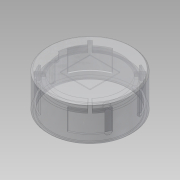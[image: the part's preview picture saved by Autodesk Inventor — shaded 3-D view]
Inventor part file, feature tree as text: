
AUTODESK INVENTOR PART (.ipt)
format: ipt  version: 2015 SP2 (Build 190223200, 223)  size: 409,600 bytes
history: native  units: mm
features: other x6, sketch x6, extrude x5, chamfer x4, projected_geometry x3, revolve x2, plane x2, pattern_circular x2
ambient origin geometry x8: Origin, YZ Plane, XZ Plane, XY Plane, X Axis, Y Axis, Z Axis, Center Point
bodies: Solid1 (feature_tree)
feature tree (30):
  other  "CrossSection1"
  other  "CrossSection2"
  other  "CrossSection3"
  other  "CrossSection4"
  other  "CrossSection5"
  revolve  "Revolution1"  Angle=90.0deg
  plane  "Work Plane3"
  chamfer  "Chamfer1"  Distance=7.75mm
  extrude  "Extrusion3"  Depth=4.363323mm
  extrude  "Extrusion1"  Depth=1.8mm
  extrude  "Extrusion6"  Depth=10.0mm
  plane  "Work Plane1"
  other  "Work Axis1"
  revolve  "Revolution2"  [1 undecoded]
  pattern_circular  "Circular Pattern1"  [2 undecoded]
  extrude  "Extrusion7"  Depth=10.0mm
  pattern_circular  "Circular Pattern3"  Count=4 Angle=360.0deg
  chamfer  "Chamfer2"  Distance=1.0mm
  extrude  "Extrusion10"  Depth=10.0mm
  chamfer  "Chamfer3"  Distance=1.5mm
  chamfer  "Chamfer4"  Distance=1.25mm
  sketch  "Sketch2"  dims[d3=12.0mm d4=90.0deg]
  sketch  "Sketch3"  dims[d5=28.0mm d15=7.75mm d16=0.0mm]
  sketch  "Sketch7"  dims[d17=4.363323mm d18=4.363323mm]
  sketch  "Sketch9"  dims[d21=0.5mm d22=2.0mm d23=45.0deg d33=1.8mm]
  sketch  "Sketch16"  dims[d35=10.0mm d36=10.0mm]
  projected_geometry  "Projected Loop2"
  projected_geometry  "Projected Loop4"
  sketch  "Sketch19"  dims[d37=0.25mm d38=0.0mm d48=0.5mm d49=2.0mm d50=7.0mm d51=20.0mm d52=0.5mm d53=2.0mm d54=0.0mm d55=20.0mm d59=0.5mm d60=7.0mm d63=8.37758mm d65=40.0mm d66=360.0deg d81=0.5mm d82=2.0mm d83=0.0mm d84=20.0mm d85=0.5mm d86=2.0mm d87=2.5mm d88=20.0mm d89=0.5mm d90=2.0mm d91=2.5mm d92=20.0mm d100=1.0mm d113=1.0mm d119=1.5mm d120=1.25mm d121=4.363323mm d122=4.363323mm d123=6.75mm d124=0.0mm d127=0.872665mm d128=0.436332mm d129=0.872665mm d130=6.75mm d131=0.0mm d132=40.0mm d133=360.0deg d135=0.125mm d136=0.25mm d137=45.0deg d140=21.0mm d141=23.0mm d143=0.5mm d144=2.0mm d145=45.0deg d148=1.8mm d149=0.5mm d150=2.0mm d151=45.0deg d152=1.25mm d153=12.75mm d154=12.75mm d155=25.5mm d158=10.0mm d159=0.0mm d160=8.37758mm d161=12.0mm d162=6.0mm]
  projected_geometry  "Projected Loop5"
note: 3 required parameter values undecoded (feature->parameter linkage not recoverable at this tier; creation-order binding heuristic only, values carry confidence <= 0.55)